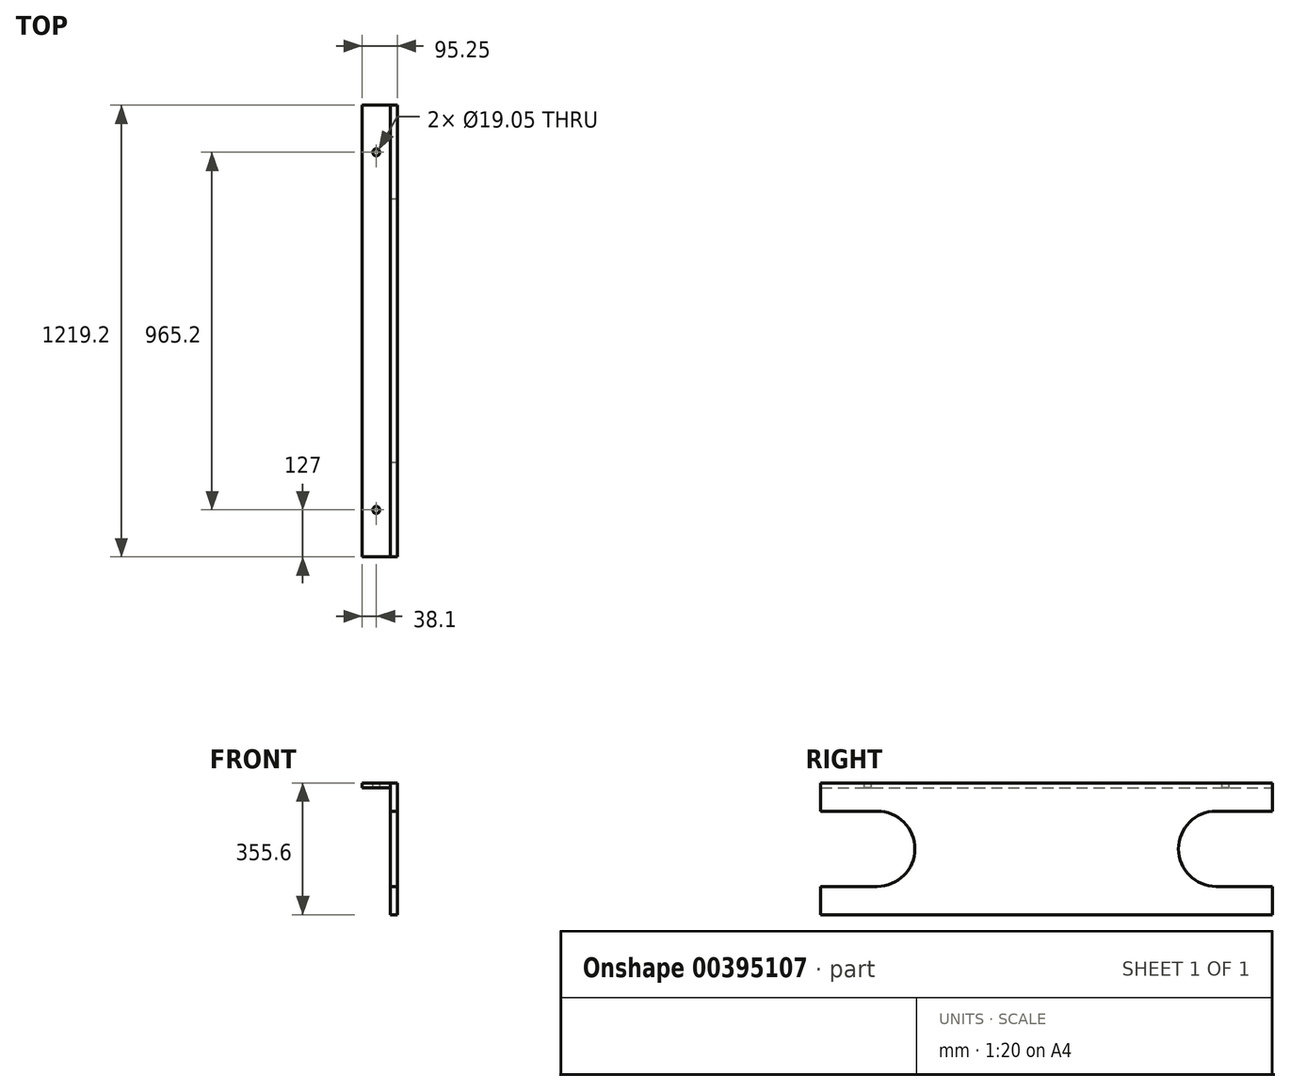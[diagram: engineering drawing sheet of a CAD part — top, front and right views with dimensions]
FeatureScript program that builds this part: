
annotation { "Feature Type Name" : "Feature", "Feature Type Description" : "" }
export const myFeature = defineFeature(function(context is Context, id is Id, definition is map)
    precondition{}
    {
        {
            var Q0;
            Q0=qCreatedBy(makeId("Right.planeOp"),FACE);
            var sketch = newSketch(context, id + "F0", { "sketchPlane" : qUnion([Q0])});
            skLineSegment(sketch, "E0.bottom", {"start": v(-609.6, 177.8) * mm, "end": v(609.6, 177.8) * mm});
            skLineSegment(sketch, "E0.top", {"start": v(-609.6, -177.8) * mm, "end": v(609.6, -177.8) * mm});
            skLineSegment(sketch, "E0.left", {"start": v(-609.6, 177.8) * mm, "end": v(-609.6, 101.6) * mm});
            skLineSegment(sketch, "E0.right", {"start": v(609.6, 177.8) * mm, "end": v(609.6, 101.6) * mm});
            skPoint(sketch, "E0.middle", {"position": v(0, 0) * mm});
            skLineSegment(sketch, "E1", {"start": v(-609.6, 0) * mm, "end": v(609.6, 0) * mm, "construction": true});
            skArc(sketch, "E2", {"start": v(-457.2, -101.6) * mm, "mid": v(-355.6, 0) * mm, "end": v(-457.2, 101.6) * mm});
            skLineSegment(sketch, "E3", {"start": v(-457.2, 101.6) * mm, "end": v(-609.6, 101.6) * mm});
            skLineSegment(sketch, "E4", {"start": v(-457.2, -101.6) * mm, "end": v(-609.6, -101.6) * mm});
            skLineSegment(sketch, "E5.trimOffspring", {"start": v(-609.6, -101.6) * mm, "end": v(-609.6, -177.8) * mm});
            skLineSegment(sketch, "E6", {"start": v(0, 177.8) * mm, "end": v(0, -177.8) * mm, "construction": true});
            skLineSegment(sketch, "E7.MirrorCS", {"start": v(457.2, -101.6) * mm, "end": v(609.6, -101.6) * mm});
            skArc(sketch, "E8.MirrorCS", {"start": v(457.2, -101.6) * mm, "mid": v(355.6, 0) * mm, "end": v(457.2, 101.6) * mm});
            skLineSegment(sketch, "E9.MirrorCS", {"start": v(457.2, 101.6) * mm, "end": v(609.6, 101.6) * mm});
            skLineSegment(sketch, "E10.trimOffspring", {"start": v(609.6, -101.6) * mm, "end": v(609.6, -177.8) * mm});
            skSolve(sketch);
        }
        {
            var Q0;
            Q0 = qSketchRegion(id + "F0", true);
            extrude(context, id + "F1", {"entities" : qUnion([Q0]), "depth" : 19.05 * mm});
        }
        {
            var Q0;
            Q0=makeQuery(id+"F1.opExtrude","SWEPT_FACE",FACE,{"disambiguationData":[OSD([sQuery(id+"F0.wireOp",EDGE,"E0.bottom")])]});
            var sketch = newSketch(context, id + "F2", { "sketchPlane" : qUnion([Q0])});
            skLineSegment(sketch, "E11.0", {"start": v(0, -609.6) * mm, "end": v(0, 609.6) * mm});
            skLineSegment(sketch, "E12.0", {"start": v(-76.2, -609.6) * mm, "end": v(-76.2, 609.6) * mm});
            skLineSegment(sketch, "E13", {"start": v(0, 609.6) * mm, "end": v(-76.2, 609.6) * mm});
            skLineSegment(sketch, "E14", {"start": v(-76.2, -609.6) * mm, "end": v(0, -609.6) * mm});
            skLineSegment(sketch, "E15", {"start": v(-38.1, -609.6) * mm, "end": v(-38.1, 609.6) * mm, "construction": true});
            skCircle(sketch, "E16", {"center": v(-38.1, -482.6) * mm, "radius": 9.52 * mm});
            skLineSegment(sketch, "E17", {"start": v(0, 0) * mm, "end": v(-76.2, 0) * mm, "construction": true});
            skCircle(sketch, "E18.MirrorC", {"center": v(-38.1, 482.6) * mm, "radius": 9.52 * mm});
            skSolve(sketch);
        }
        {
            var Q0;
            Q0 = qSketchRegion(id + "F2", true);
            extrude(context, id + "F3", {"entities" : qUnion([Q0]), "oppositeDirection" : true, "depth" : 12.7 * mm});
        }
    });
